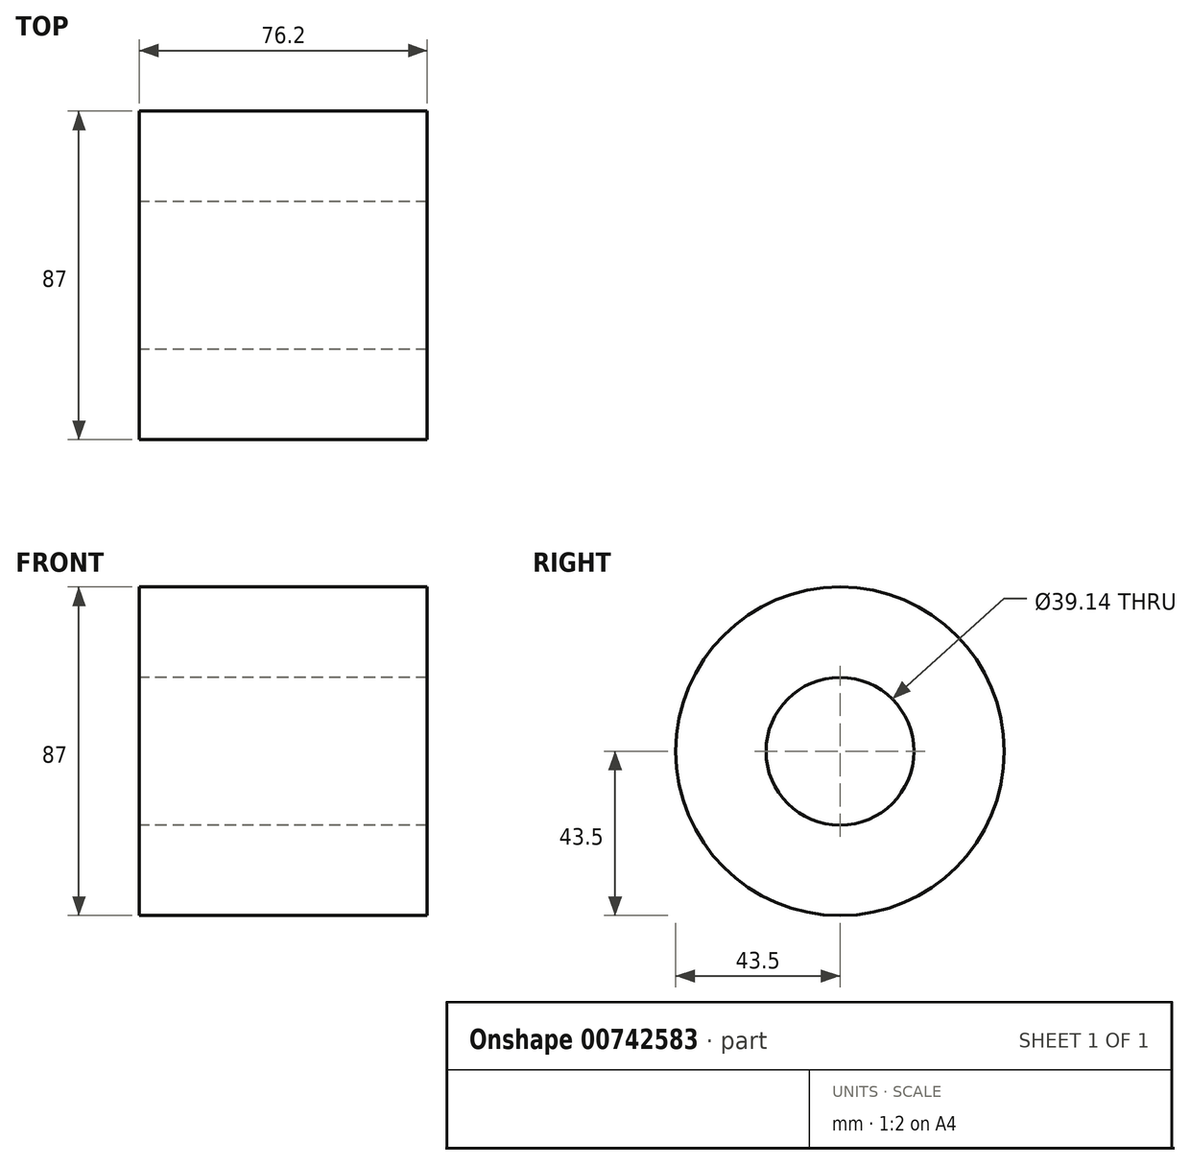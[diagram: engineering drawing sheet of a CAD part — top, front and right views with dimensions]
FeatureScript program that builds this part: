
annotation { "Feature Type Name" : "Feature", "Feature Type Description" : "" }
export const myFeature = defineFeature(function(context is Context, id is Id, definition is map)
    precondition{}
    {
        {
            var Q0;
            Q0=qCreatedBy(makeId("Right.planeOp"),FACE);
            var sketch = newSketch(context, id + "F0", { "sketchPlane" : qUnion([Q0])});
            skCircle(sketch, "E0", {"center": v(0, 0) * mm, "radius": 43.5 * mm});
            skCircle(sketch, "E1", {"center": v(0, 0) * mm, "radius": 19.57 * mm});
            skSolve(sketch);
        }
        {
            var Q0;
            Q0 = qSketchRegion(id + "F0", true);
            extrude(context, id + "F1", {"entities" : qUnion([Q0]), "depth" : 76.2 * mm, "offsetDistance" : 25.4 * mm});
        }
    });
